# Revit family: LC8ML
name_source: partatom
category: Lighting Fixtures
revit_build: Autodesk Revit 2014 (Build: 20130308_1515(x64)
units: mm (PartAtom-declared; Revit-internal decimal feet)

## types (1)
- LC8HL
    Apparent Load = 52 VA
    Ceiling Cutout = 8 1/2"
    Color Filter = 16777215
    Connector Description = Lighting Connector
    Cutout Radius = 4"
    Default Elevation = 48"
    Description = 8 Inch Medium Lumen LED Downlight
    Dimming Lamp Color Temperature Shift = <None>
    Emit Shape Visible in Rendering = Yes
    Emit from Circle Diameter = 8"
    Frequency = 60 Hz
    Housing Options = 0-10V dimming to 10%
    Input Current = 245 A
    Is 120V = Yes
    Is 277V = No
    Lamp = 8 Inch commercial grade high lumen LED downlight
    Load Classification = Lighting
    Manufacturer = Prescolite
    Model = LC8ML
    Photometric Web File = LC8ML_8LCML30L35K8.ies
    Product Documentation Link = https://hubbellcdn.com
    Product Material = Metal - Hubbell - Stainless Steel
    Product Page URL = https://www.hubbell.com
    Reflector Finish = Paint - Hubbell - White
    Tilt Angle = -90.00°
    Trim Aperture = 8 inch Open Reflector/Light EngineAssembly
    URL = http://www.prescolite.com
    Voltage = 120 V
    Wattage Comments = 52-68 W

## geometry (parser evidence)
native form markers: Blend x2, Sweep x3
no freeform markers — native parametric forms only
